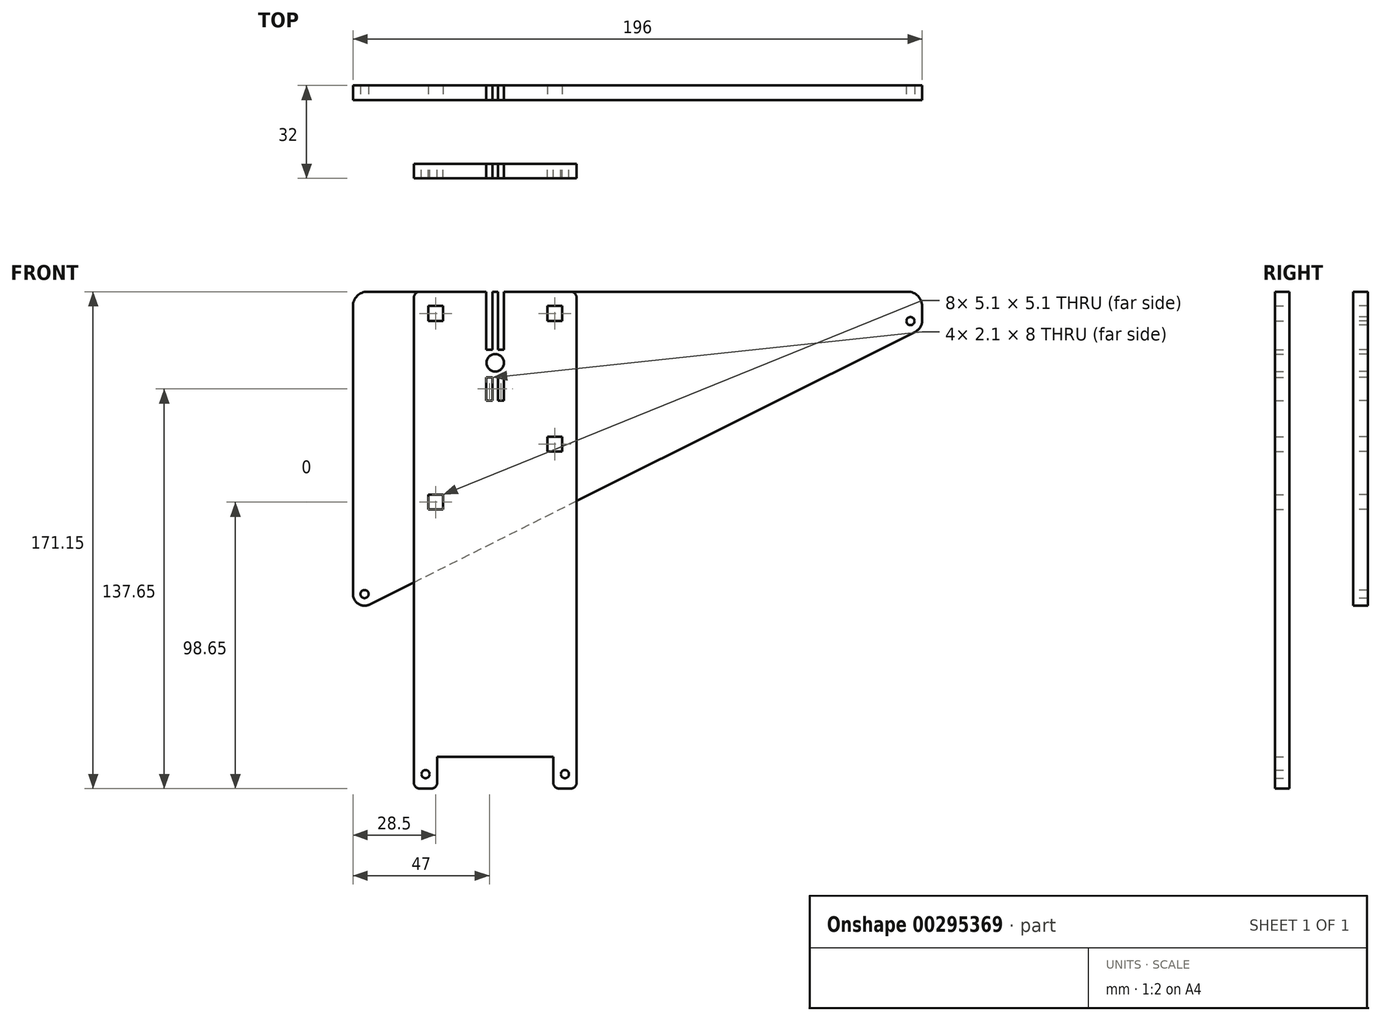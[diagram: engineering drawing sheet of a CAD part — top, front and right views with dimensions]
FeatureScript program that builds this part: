
annotation { "Feature Type Name" : "Feature", "Feature Type Description" : "" }
export const myFeature = defineFeature(function(context is Context, id is Id, definition is map)
    precondition{}
    {
        {
            var Q0;
            Q0=qCreatedBy(makeId("Front.planeOp"),FACE);
            var sketch = newSketch(context, id + "F0", { "sketchPlane" : qUnion([Q0])});
            skArc(sketch, "E0", {"start": v(144.79, 157.42) * mm, "mid": v(146.4, 158.9) * mm, "end": v(147, 161) * mm});
            skLineSegment(sketch, "E1.trimOffspring", {"start": v(142.05, 171.15) * mm, "end": v(3.05, 171.15) * mm});
            skLineSegment(sketch, "E2", {"start": v(-49, 67) * mm, "end": v(-49, 166.15) * mm});
            skCircle(sketch, "E3", {"center": v(-45, 67) * mm, "radius": 1.4 * mm});
            skCircle(sketch, "E4", {"center": v(143, 161) * mm, "radius": 1.4 * mm});
            skArc(sketch, "E5", {"start": v(-49, 67) * mm, "mid": v(-47.1, 63.6) * mm, "end": v(-43.21, 63.42) * mm});
            skLineSegment(sketch, "E6", {"start": v(-43.21, 63.42) * mm, "end": v(144.79, 157.42) * mm});
            skLineSegment(sketch, "E7", {"start": v(147, 166.15) * mm, "end": v(147, 161) * mm});
            skArc(sketch, "E8.filletArc", {"start": v(-44, 171.15) * mm, "mid": v(-47.54, 169.69) * mm, "end": v(-49, 166.15) * mm});
            skPoint(sketch, "E9.visualSharp", {"position": v(147, 171) * mm});
            skArc(sketch, "E9.filletArc", {"start": v(147, 166.15) * mm, "mid": v(145.55, 169.67) * mm, "end": v(142.05, 171.15) * mm});
            skCircle(sketch, "E10", {"center": v(0, 146.65) * mm, "radius": 3 * mm});
            skLineSegment(sketch, "E11.top", {"start": v(-3.05, 151.15) * mm, "end": v(-0.95, 151.15) * mm});
            skLineSegment(sketch, "E11.left", {"start": v(-3.05, 171.15) * mm, "end": v(-3.05, 151.15) * mm});
            skLineSegment(sketch, "E11.right", {"start": v(-0.95, 171.15) * mm, "end": v(-0.95, 151.15) * mm});
            skLineSegment(sketch, "E12.bottom", {"start": v(-3.05, 141.65) * mm, "end": v(-0.95, 141.65) * mm});
            skLineSegment(sketch, "E12.top", {"start": v(-3.05, 133.65) * mm, "end": v(-0.95, 133.65) * mm});
            skLineSegment(sketch, "E12.left", {"start": v(-3.05, 141.65) * mm, "end": v(-3.05, 133.65) * mm});
            skLineSegment(sketch, "E12.right", {"start": v(-0.95, 141.65) * mm, "end": v(-0.95, 133.65) * mm});
            skLineSegment(sketch, "E13.MirrorCS", {"start": v(3.05, 133.65) * mm, "end": v(0.95, 133.65) * mm});
            skLineSegment(sketch, "E14.MirrorCS", {"start": v(3.05, 141.65) * mm, "end": v(0.95, 141.65) * mm});
            skLineSegment(sketch, "E15.MirrorCS", {"start": v(0.95, 171.15) * mm, "end": v(0.95, 151.15) * mm});
            skLineSegment(sketch, "E16.MirrorCS", {"start": v(3.05, 151.15) * mm, "end": v(0.95, 151.15) * mm});
            skLineSegment(sketch, "E17.MirrorCS", {"start": v(3.05, 141.65) * mm, "end": v(3.05, 133.65) * mm});
            skLineSegment(sketch, "E18.MirrorCS", {"start": v(0.95, 141.65) * mm, "end": v(0.95, 133.65) * mm});
            skLineSegment(sketch, "E19.MirrorCS", {"start": v(3.05, 171.15) * mm, "end": v(3.05, 151.15) * mm});
            skLineSegment(sketch, "E20.trimOffspring", {"start": v(-3.05, 171.15) * mm, "end": v(-44, 171.15) * mm});
            skLineSegment(sketch, "E21.trimOffspring", {"start": v(0.95, 171.15) * mm, "end": v(-0.95, 171.15) * mm});
            skLineSegment(sketch, "E22.bottom", {"start": v(-23.05, 166.2) * mm, "end": v(-17.95, 166.2) * mm});
            skLineSegment(sketch, "E22.top", {"start": v(-23.05, 161.1) * mm, "end": v(-17.95, 161.1) * mm});
            skLineSegment(sketch, "E22.left", {"start": v(-23.05, 166.2) * mm, "end": v(-23.05, 161.1) * mm});
            skLineSegment(sketch, "E22.right", {"start": v(-17.95, 166.2) * mm, "end": v(-17.95, 161.1) * mm});
            skLineSegment(sketch, "E23.bottom", {"start": v(17.95, 166.2) * mm, "end": v(23.05, 166.2) * mm});
            skLineSegment(sketch, "E23.top", {"start": v(17.95, 161.1) * mm, "end": v(23.05, 161.1) * mm});
            skLineSegment(sketch, "E23.left", {"start": v(17.95, 166.2) * mm, "end": v(17.95, 161.1) * mm});
            skLineSegment(sketch, "E23.right", {"start": v(23.05, 166.2) * mm, "end": v(23.05, 161.1) * mm});
            skLineSegment(sketch, "E24.bottom", {"start": v(-23.05, 101.2) * mm, "end": v(-17.95, 101.2) * mm});
            skLineSegment(sketch, "E24.top", {"start": v(-23.05, 96.1) * mm, "end": v(-17.95, 96.1) * mm});
            skLineSegment(sketch, "E24.left", {"start": v(-23.05, 101.2) * mm, "end": v(-23.05, 96.1) * mm});
            skLineSegment(sketch, "E24.right", {"start": v(-17.95, 101.2) * mm, "end": v(-17.95, 96.1) * mm});
            skLineSegment(sketch, "E25.bottom", {"start": v(23.05, 121.2) * mm, "end": v(17.95, 121.2) * mm});
            skLineSegment(sketch, "E25.top", {"start": v(23.05, 116.1) * mm, "end": v(17.95, 116.1) * mm});
            skLineSegment(sketch, "E25.left", {"start": v(23.05, 121.2) * mm, "end": v(23.05, 116.1) * mm});
            skLineSegment(sketch, "E25.right", {"start": v(17.95, 121.2) * mm, "end": v(17.95, 116.1) * mm});
            skPoint(sketch, "E26", {"position": v(-20.5, 166.2) * mm});
            skPoint(sketch, "E27", {"position": v(20.5, 166.2) * mm});
            skPoint(sketch, "E28", {"position": v(23.05, 163.65) * mm});
            skPoint(sketch, "E29", {"position": v(-23.05, 163.65) * mm});
            skPoint(sketch, "E30", {"position": v(-23.05, 98.65) * mm});
            skPoint(sketch, "E31", {"position": v(17.95, 118.65) * mm});
            skPoint(sketch, "E32.middle.positionSnap0", {"position": v(23.05, 118.65) * mm});
            skPoint(sketch, "E32.centerSnap0", {"position": v(23.05, 118.65) * mm});
            skPoint(sketch, "E33", {"position": v(0, 0) * mm});
            skPoint(sketch, "E34.centerSnap0", {"position": v(0, 171.15) * mm});
            skSolve(sketch);
        }
        {
            var Q0;
            Q0=qCreatedBy(makeId("Front.planeOp"),FACE);
            cPlane(context, id + "F1", {"entities" : qUnion([Q0]), "cplaneType" : CPlaneType.OFFSET, "offset" : (17 + 5) * mm, "width" : 150 * mm, "height" : 150 * mm});
        }
        {
            var Q0;
            Q0=qCreatedBy(id+"F1.planeOp",FACE);
            var sketch = newSketch(context, id + "F2", { "sketchPlane" : qUnion([Q0])});
            skPoint(sketch, "E35", {"position": v(0, 0) * mm});
            skCircle(sketch, "E36", {"center": v(-24, 5) * mm, "radius": 1.4 * mm});
            skCircle(sketch, "E37", {"center": v(24, 5) * mm, "radius": 1.4 * mm});
            skLineSegment(sketch, "E38", {"start": v(-26, 0) * mm, "end": v(-22, 0) * mm});
            skLineSegment(sketch, "E39.trimOffspring", {"start": v(22, 0) * mm, "end": v(26, 0) * mm});
            skLineSegment(sketch, "E40.top", {"start": v(-20, 11) * mm, "end": v(20, 11) * mm});
            skLineSegment(sketch, "E40.left", {"start": v(-20, 2) * mm, "end": v(-20, 11) * mm});
            skLineSegment(sketch, "E40.right", {"start": v(20, 2) * mm, "end": v(20, 11) * mm});
            skPoint(sketch, "E40.middle", {"position": v(0, 5.5) * mm});
            skLineSegment(sketch, "E41", {"start": v(-28, 2) * mm, "end": v(-28, 169.15) * mm});
            skLineSegment(sketch, "E42", {"start": v(-26, 171.15) * mm, "end": v(-3.05, 171.15) * mm});
            skLineSegment(sketch, "E43", {"start": v(28, 169.15) * mm, "end": v(28, 2) * mm});
            skLineSegment(sketch, "E44.bottom", {"start": v(-23.05, 166.2) * mm, "end": v(-17.95, 166.2) * mm});
            skLineSegment(sketch, "E44.top", {"start": v(-23.05, 161.1) * mm, "end": v(-17.95, 161.1) * mm});
            skLineSegment(sketch, "E44.left", {"start": v(-23.05, 166.2) * mm, "end": v(-23.05, 161.1) * mm});
            skLineSegment(sketch, "E44.right", {"start": v(-17.95, 166.2) * mm, "end": v(-17.95, 161.1) * mm});
            skLineSegment(sketch, "E45.bottom", {"start": v(17.95, 166.2) * mm, "end": v(23.05, 166.2) * mm});
            skLineSegment(sketch, "E45.top", {"start": v(17.95, 161.1) * mm, "end": v(23.05, 161.1) * mm});
            skLineSegment(sketch, "E45.left", {"start": v(17.95, 166.2) * mm, "end": v(17.95, 161.1) * mm});
            skLineSegment(sketch, "E45.right", {"start": v(23.05, 166.2) * mm, "end": v(23.05, 161.1) * mm});
            skLineSegment(sketch, "E46.bottom", {"start": v(-23.05, 101.2) * mm, "end": v(-17.95, 101.2) * mm});
            skLineSegment(sketch, "E46.top", {"start": v(-23.05, 96.1) * mm, "end": v(-17.95, 96.1) * mm});
            skLineSegment(sketch, "E46.left", {"start": v(-23.05, 101.2) * mm, "end": v(-23.05, 96.1) * mm});
            skLineSegment(sketch, "E46.right", {"start": v(-17.95, 101.2) * mm, "end": v(-17.95, 96.1) * mm});
            skLineSegment(sketch, "E47.bottom", {"start": v(23.05, 121.2) * mm, "end": v(17.95, 121.2) * mm});
            skLineSegment(sketch, "E47.top", {"start": v(23.05, 116.1) * mm, "end": v(17.95, 116.1) * mm});
            skLineSegment(sketch, "E47.left", {"start": v(23.05, 121.2) * mm, "end": v(23.05, 116.1) * mm});
            skLineSegment(sketch, "E47.right", {"start": v(17.95, 121.2) * mm, "end": v(17.95, 116.1) * mm});
            skCircle(sketch, "E48", {"center": v(0, 146.65) * mm, "radius": 3 * mm});
            skPoint(sketch, "E48.centerSnap0", {"position": v(0, 171.15) * mm});
            skLineSegment(sketch, "E49.top", {"start": v(-3.05, 151.15) * mm, "end": v(-0.95, 151.15) * mm});
            skLineSegment(sketch, "E49.left", {"start": v(-3.05, 171.15) * mm, "end": v(-3.05, 151.15) * mm});
            skLineSegment(sketch, "E49.right", {"start": v(-0.95, 171.15) * mm, "end": v(-0.95, 151.15) * mm});
            skLineSegment(sketch, "E50.bottom", {"start": v(-3.05, 141.65) * mm, "end": v(-0.95, 141.65) * mm});
            skLineSegment(sketch, "E50.top", {"start": v(-3.05, 133.65) * mm, "end": v(-0.95, 133.65) * mm});
            skLineSegment(sketch, "E50.left", {"start": v(-3.05, 141.65) * mm, "end": v(-3.05, 133.65) * mm});
            skLineSegment(sketch, "E50.right", {"start": v(-0.95, 141.65) * mm, "end": v(-0.95, 133.65) * mm});
            skLineSegment(sketch, "E51.MirrorCS", {"start": v(3.05, 133.65) * mm, "end": v(0.95, 133.65) * mm});
            skLineSegment(sketch, "E52.MirrorCS", {"start": v(3.05, 141.65) * mm, "end": v(0.95, 141.65) * mm});
            skLineSegment(sketch, "E53.MirrorCS", {"start": v(0.95, 171.15) * mm, "end": v(0.95, 151.15) * mm});
            skLineSegment(sketch, "E54.MirrorCS", {"start": v(3.05, 151.15) * mm, "end": v(0.95, 151.15) * mm});
            skLineSegment(sketch, "E55.MirrorCS", {"start": v(3.05, 141.65) * mm, "end": v(3.05, 133.65) * mm});
            skLineSegment(sketch, "E56.MirrorCS", {"start": v(0.95, 141.65) * mm, "end": v(0.95, 133.65) * mm});
            skLineSegment(sketch, "E57.MirrorCS", {"start": v(3.05, 171.15) * mm, "end": v(3.05, 151.15) * mm});
            skLineSegment(sketch, "E58.trimOffspring", {"start": v(0.95, 171.15) * mm, "end": v(-0.95, 171.15) * mm});
            skLineSegment(sketch, "E59.trimOffspring", {"start": v(3.05, 171.15) * mm, "end": v(26, 171.15) * mm});
            skPoint(sketch, "E60.visualSharp", {"position": v(-28, 0) * mm});
            skArc(sketch, "E60.filletArc", {"start": v(-28, 2) * mm, "mid": v(-27.41, 0.59) * mm, "end": v(-26, 0) * mm});
            skPoint(sketch, "E61.visualSharp", {"position": v(-20, 0) * mm});
            skArc(sketch, "E61.filletArc", {"start": v(-22, 0) * mm, "mid": v(-20.59, 0.59) * mm, "end": v(-20, 2) * mm});
            skPoint(sketch, "E62.visualSharp", {"position": v(20, 0) * mm});
            skArc(sketch, "E62.filletArc", {"start": v(20, 2) * mm, "mid": v(20.59, 0.59) * mm, "end": v(22, 0) * mm});
            skPoint(sketch, "E63.visualSharp", {"position": v(28, 0) * mm});
            skArc(sketch, "E63.filletArc", {"start": v(26, 0) * mm, "mid": v(27.41, 0.59) * mm, "end": v(28, 2) * mm});
            skPoint(sketch, "E64.visualSharp", {"position": v(-28, 171.15) * mm});
            skArc(sketch, "E64.filletArc", {"start": v(-26, 171.15) * mm, "mid": v(-27.41, 170.56) * mm, "end": v(-28, 169.15) * mm});
            skPoint(sketch, "E65.visualSharp", {"position": v(28, 171.15) * mm});
            skArc(sketch, "E65.filletArc", {"start": v(28, 169.15) * mm, "mid": v(27.41, 170.56) * mm, "end": v(26, 171.15) * mm});
            skPoint(sketch, "E66", {"position": v(-20.5, 166.2) * mm});
            skPoint(sketch, "E67", {"position": v(20.5, 166.2) * mm});
            skPoint(sketch, "E68", {"position": v(23.05, 163.65) * mm});
            skPoint(sketch, "E69", {"position": v(-23.05, 163.65) * mm});
            skPoint(sketch, "E70", {"position": v(-23.05, 98.65) * mm});
            skPoint(sketch, "E71", {"position": v(17.95, 118.65) * mm});
            skLineSegment(sketch, "E72", {"start": v(38, 171.15) * mm, "end": v(38, 166.15) * mm});
            skLineSegment(sketch, "E73.bottom", {"start": v(38, 161.15) * mm, "end": v(33, 161.15) * mm});
            skLineSegment(sketch, "E73.top", {"start": v(38, 166.15) * mm, "end": v(33, 166.15) * mm});
            skLineSegment(sketch, "E73.right", {"start": v(33, 161.15) * mm, "end": v(33, 166.15) * mm});
            skPoint(sketch, "E73.middle", {"position": v(35.5, 163.65) * mm});
            skLineSegment(sketch, "E74.bottom", {"start": v(38, 116.15) * mm, "end": v(33, 116.15) * mm});
            skLineSegment(sketch, "E74.top", {"start": v(38, 121.15) * mm, "end": v(33, 121.15) * mm});
            skLineSegment(sketch, "E74.right", {"start": v(33, 116.15) * mm, "end": v(33, 121.15) * mm});
            skPoint(sketch, "E74.middle", {"position": v(35.5, 118.65) * mm});
            skPoint(sketch, "E74.middle.positionSnap0", {"position": v(23.05, 118.65) * mm});
            skPoint(sketch, "E74.centerSnap0", {"position": v(23.05, 118.65) * mm});
            skLineSegment(sketch, "E75.bottom", {"start": v(-40, 166.15) * mm, "end": v(-35, 166.15) * mm});
            skLineSegment(sketch, "E75.top", {"start": v(-40, 161.15) * mm, "end": v(-35, 161.15) * mm});
            skLineSegment(sketch, "E75.right", {"start": v(-35, 166.15) * mm, "end": v(-35, 161.15) * mm});
            skPoint(sketch, "E75.middle", {"position": v(-37.5, 163.65) * mm});
            skLineSegment(sketch, "E76.bottom", {"start": v(-40, 101.15) * mm, "end": v(-35, 101.15) * mm});
            skLineSegment(sketch, "E76.top", {"start": v(-40, 96.15) * mm, "end": v(-35, 96.15) * mm});
            skLineSegment(sketch, "E76.right", {"start": v(-35, 101.15) * mm, "end": v(-35, 96.15) * mm});
            skPoint(sketch, "E76.middle", {"position": v(-37.5, 98.65) * mm});
            skLineSegment(sketch, "E77.trimOffspring", {"start": v(38, 161.15) * mm, "end": v(38, 121.15) * mm});
            skLineSegment(sketch, "E78.trimOffspring", {"start": v(38, 116.15) * mm, "end": v(38, 111.15) * mm});
            skLineSegment(sketch, "E79", {"start": v(38, 171.15) * mm, "end": v(59, 171.15) * mm});
            skLineSegment(sketch, "E80", {"start": v(59, 171.15) * mm, "end": v(59, 166.15) * mm});
            skLineSegment(sketch, "E81", {"start": v(59, 166.15) * mm, "end": v(64, 166.15) * mm});
            skLineSegment(sketch, "E82", {"start": v(64, 166.15) * mm, "end": v(64, 161.15) * mm});
            skLineSegment(sketch, "E83", {"start": v(64, 161.15) * mm, "end": v(59, 161.15) * mm});
            skLineSegment(sketch, "E84", {"start": v(59, 161.15) * mm, "end": v(59, 121.15) * mm});
            skLineSegment(sketch, "E85", {"start": v(59, 121.15) * mm, "end": v(64, 121.15) * mm});
            skLineSegment(sketch, "E86", {"start": v(64, 121.15) * mm, "end": v(64, 116.15) * mm});
            skLineSegment(sketch, "E87", {"start": v(64, 116.15) * mm, "end": v(59, 116.15) * mm});
            skLineSegment(sketch, "E88", {"start": v(59, 116.15) * mm, "end": v(59, 111.15) * mm});
            skLineSegment(sketch, "E89", {"start": v(59, 111.15) * mm, "end": v(38, 111.15) * mm});
            skLineSegment(sketch, "E90.trimOffspring", {"start": v(-40, 161.15) * mm, "end": v(-40, 101.15) * mm});
            skPoint(sketch, "E91.start.orphan", {"position": v(-40, 171.15) * mm});
            skLineSegment(sketch, "E92.trimOffspring", {"start": v(-40, 96.15) * mm, "end": v(-40, 91.15) * mm});
            skLineSegment(sketch, "E93", {"start": v(-40, 166.15) * mm, "end": v(-40, 171.15) * mm});
            skLineSegment(sketch, "E94", {"start": v(-40, 171.15) * mm, "end": v(-61, 171.15) * mm});
            skLineSegment(sketch, "E95", {"start": v(-61, 171.15) * mm, "end": v(-61, 166.15) * mm});
            skLineSegment(sketch, "E96", {"start": v(-61, 166.15) * mm, "end": v(-66, 166.15) * mm});
            skLineSegment(sketch, "E97", {"start": v(-66, 166.15) * mm, "end": v(-66, 161.15) * mm});
            skPoint(sketch, "E97.endSnap0", {"position": v(-37.5, 161.15) * mm});
            skLineSegment(sketch, "E98", {"start": v(-66, 161.15) * mm, "end": v(-61, 161.15) * mm});
            skLineSegment(sketch, "E99", {"start": v(-61, 161.15) * mm, "end": v(-61, 101.15) * mm});
            skLineSegment(sketch, "E100", {"start": v(-61, 101.15) * mm, "end": v(-66, 101.15) * mm});
            skLineSegment(sketch, "E101", {"start": v(-66, 101.15) * mm, "end": v(-66, 96.15) * mm});
            skLineSegment(sketch, "E102", {"start": v(-66, 96.15) * mm, "end": v(-61, 96.15) * mm});
            skLineSegment(sketch, "E103", {"start": v(-61, 96.15) * mm, "end": v(-61, 91.15) * mm});
            skLineSegment(sketch, "E104", {"start": v(-61, 91.15) * mm, "end": v(-40, 91.15) * mm});
            skSolve(sketch);
        }
        {
            var Q0;
            Q0=makeQuery(id+"F0.imprint","IMPRINT",FACE,{"disambiguationData":[TD([[makeQuery(id+"F0.imprint","IMPRINT",EDGE,{"derivedFrom":sQuery(id+"F0.wireOp",EDGE,"E0")}),1.0]])]});
            extrude(context, id + "F3", {"entities" : qUnion([Q0]), "oppositeDirection" : true, "depth" : 5 * mm});
        }
        {
            var Q0;
            Q0=makeQuery(id+"F2.imprint","IMPRINT",FACE,{"disambiguationData":[TD([[makeQuery(id+"F2.imprint","IMPRINT",EDGE,{"derivedFrom":sQuery(id+"F2.wireOp",EDGE,"E36")}),-1.0]])]});
            extrude(context, id + "F4", {"entities" : qUnion([Q0]), "depth" : 5 * mm});
        }
    });
